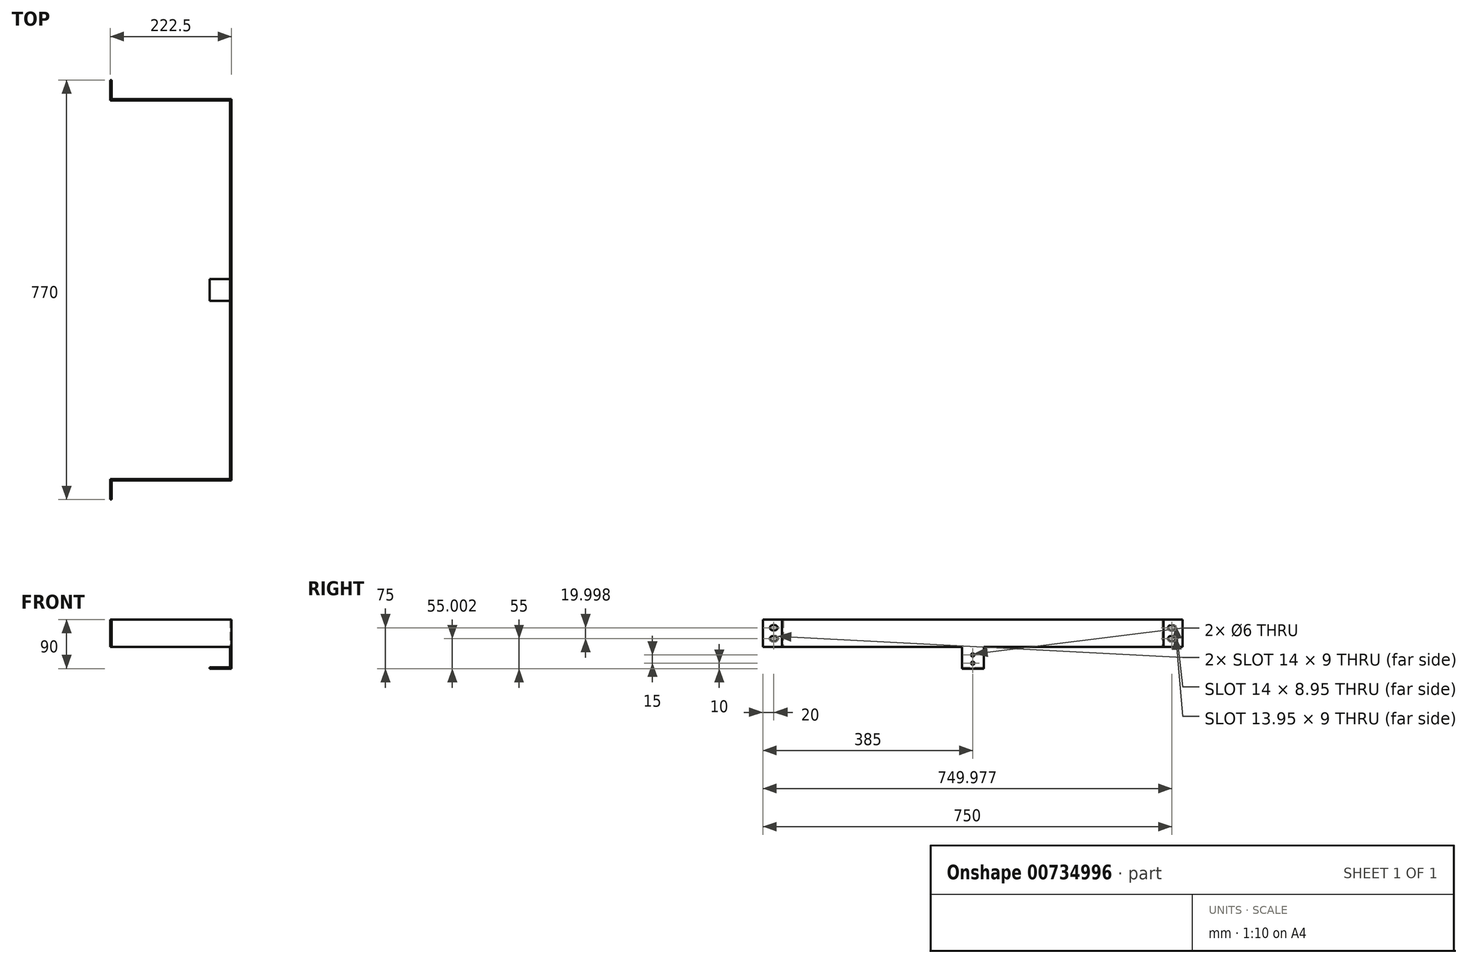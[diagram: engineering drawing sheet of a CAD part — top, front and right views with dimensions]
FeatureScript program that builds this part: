
annotation { "Feature Type Name" : "Feature", "Feature Type Description" : "" }
export const myFeature = defineFeature(function(context is Context, id is Id, definition is map)
    precondition{}
    {
        {
            var Q0;
            Q0=qCreatedBy(makeId("Top.planeOp"),FACE);
            var sketch = newSketch(context, id + "F0", { "sketchPlane" : qUnion([Q0])});
            skLineSegment(sketch, "E0", {"start": v(0, 0) * mm, "end": v(0, 350) * mm});
            skLineSegment(sketch, "E1", {"start": v(0, 350) * mm, "end": v(-220, 350) * mm});
            skLineSegment(sketch, "E2", {"start": v(-220, 350) * mm, "end": v(-220, 385) * mm});
            skLineSegment(sketch, "E3", {"start": v(-220, 385) * mm, "end": v(-222.5, 385) * mm});
            skLineSegment(sketch, "E4", {"start": v(-222.5, 385) * mm, "end": v(-222.5, 347.5) * mm});
            skLineSegment(sketch, "E5", {"start": v(-222.5, 347.5) * mm, "end": v(-2.5, 347.5) * mm});
            skLineSegment(sketch, "E6", {"start": v(-2.5, 347.5) * mm, "end": v(-2.5, 0) * mm});
            skLineSegment(sketch, "E7", {"start": v(-2.5, 0) * mm, "end": v(0, 0) * mm});
            skLineSegment(sketch, "E8.MirrorCS", {"start": v(-220, -385) * mm, "end": v(-222.5, -385) * mm});
            skLineSegment(sketch, "E9.MirrorCS", {"start": v(0, -350) * mm, "end": v(-220, -350) * mm});
            skLineSegment(sketch, "E10.MirrorCS", {"start": v(0, 0) * mm, "end": v(0, -350) * mm});
            skLineSegment(sketch, "E11.MirrorCS", {"start": v(-2.5, -347.5) * mm, "end": v(-2.5, 0) * mm});
            skLineSegment(sketch, "E12.MirrorCS", {"start": v(-220, -350) * mm, "end": v(-220, -385) * mm});
            skLineSegment(sketch, "E13.MirrorCS", {"start": v(-222.5, -347.5) * mm, "end": v(-2.5, -347.5) * mm});
            skLineSegment(sketch, "E14.MirrorCS", {"start": v(-222.5, -385) * mm, "end": v(-222.5, -347.5) * mm});
            skSolve(sketch);
        }
        {
            var Q0;
            Q0 = qSketchRegion(id + "F0", true);
            extrude(context, id + "F1", {"entities" : qUnion([Q0]), "depth" : 50 * mm, "offsetDistance" : 25 * mm});
        }
        {
            var Q0;
            Q0=qCreatedBy(makeId("Right.planeOp"),FACE);
            var sketch = newSketch(context, id + "F2", { "sketchPlane" : qUnion([Q0])});
            skLineSegment(sketch, "E15", {"start": v(0, 0) * mm, "end": v(-20, 0) * mm});
            skLineSegment(sketch, "E16", {"start": v(-20, 0) * mm, "end": v(-20, -40) * mm});
            skLineSegment(sketch, "E17", {"start": v(-20, -40) * mm, "end": v(20, -40) * mm});
            skLineSegment(sketch, "E18", {"start": v(20, -40) * mm, "end": v(20, 0) * mm});
            skLineSegment(sketch, "E19", {"start": v(20, 0) * mm, "end": v(0, 0) * mm});
            skCircle(sketch, "E20", {"center": v(0, -30) * mm, "radius": 3 * mm});
            skCircle(sketch, "E21", {"center": v(0, -15) * mm, "radius": 3 * mm});
            skSolve(sketch);
        }
        {
            var Q0;
            Q0=makeQuery(id+"F2.imprint","IMPRINT",FACE,{"disambiguationData":[TD([[makeQuery(id+"F2.imprint","IMPRINT",EDGE,{"derivedFrom":sQuery(id+"F2.wireOp",EDGE,"E15")}),1.0]])]});
            extrude(context, id + "F3", {"entities" : qUnion([Q0]), "operationType" : NewBodyOperationType.ADD, "depth" : -2.5 * mm, "offsetDistance" : 25 * mm});
        }
        {
            var Q0;
            Q0=makeQuery(id+"F1.opExtrude","SWEPT_FACE",FACE,{"disambiguationData":[OSD([sQuery(id+"F0.wireOp",EDGE,"E12.MirrorCS")])]});
            var sketch = newSketch(context, id + "F4", { "sketchPlane" : qUnion([Q0])});
            skCircle(sketch, "E22", {"center": v(-367.5, 35) * mm, "radius": 4.5 * mm});
            skCircle(sketch, "E23", {"center": v(-367.5, 15) * mm, "radius": 4.5 * mm});
            skLineSegment(sketch, "E24", {"start": v(-367.5, 35) * mm, "end": v(-362.5, 35) * mm});
            skLineSegment(sketch, "E25", {"start": v(-367.5, 15) * mm, "end": v(-362.5, 15) * mm});
            skCircle(sketch, "E26", {"center": v(-362.5, 35) * mm, "radius": 4.5 * mm});
            skCircle(sketch, "E27", {"center": v(-362.5, 15) * mm, "radius": 4.5 * mm});
            skLineSegment(sketch, "E28", {"start": v(-367.68, 39.5) * mm, "end": v(-362.5, 39.5) * mm});
            skLineSegment(sketch, "E29", {"start": v(-367.5, 30.5) * mm, "end": v(-362.5, 30.5) * mm});
            skLineSegment(sketch, "E30", {"start": v(-367.49, 19.5) * mm, "end": v(-362.5, 19.5) * mm});
            skLineSegment(sketch, "E31", {"start": v(-367.67, 10.5) * mm, "end": v(-362.33, 10.5) * mm});
            skSolve(sketch);
        }
        {
            var Q0;
            Q0 = qSketchRegion(id + "F4", true);
            var Q1;
            {var subQ0=sQuery(id+"F4.wireOp",EDGE,"E24");var subQ1=sQuery(id+"F4.wireOp",EDGE,"E22");var subQ2=makeQuery(id+"F4.imprint","INTERSECT",VERTEX,{"derivedFrom":[subQ1,subQ0]});Q1=makeQuery(id+"F4.imprint","IMPRINT",FACE,{"disambiguationData":[TD([[makeQuery(id+"F4.imprint","IMPRINT",EDGE,{"disambiguationData":[TD([[subQ2,1.0]])],"derivedFrom":subQ1}),1.0]])]});}
            var Q2;
            {var subQ0=sQuery(id+"F4.wireOp",EDGE,"E25");var subQ1=sQuery(id+"F4.wireOp",EDGE,"E23");var subQ2=makeQuery(id+"F4.imprint","INTERSECT",VERTEX,{"derivedFrom":[subQ1,subQ0]});Q2=makeQuery(id+"F4.imprint","IMPRINT",FACE,{"disambiguationData":[TD([[makeQuery(id+"F4.imprint","IMPRINT",EDGE,{"disambiguationData":[TD([[subQ2,-1.0]])],"derivedFrom":subQ1}),1.0]])]});}
            var Q3;
            {var subQ0=sQuery(id+"F4.wireOp",EDGE,"E25");var subQ1=sQuery(id+"F4.wireOp",EDGE,"E23");var subQ2=makeQuery(id+"F4.imprint","INTERSECT",VERTEX,{"derivedFrom":[subQ1,subQ0]});Q3=makeQuery(id+"F4.imprint","IMPRINT",FACE,{"disambiguationData":[TD([[makeQuery(id+"F4.imprint","IMPRINT",EDGE,{"disambiguationData":[TD([[subQ2,1.0]])],"derivedFrom":subQ1}),1.0]])]});}
            var Q4;
            {var subQ0=sQuery(id+"F4.wireOp",EDGE,"E24");var subQ1=sQuery(id+"F4.wireOp",EDGE,"E22");var subQ2=makeQuery(id+"F4.imprint","INTERSECT",VERTEX,{"derivedFrom":[subQ1,subQ0]});Q4=makeQuery(id+"F4.imprint","IMPRINT",FACE,{"disambiguationData":[TD([[makeQuery(id+"F4.imprint","IMPRINT",EDGE,{"disambiguationData":[TD([[subQ2,-1.0]])],"derivedFrom":subQ1}),1.0]])]});}
            extrude(context, id + "F5", {"entities" : qUnion([Q0, Q1, Q2, Q3, Q4]), "operationType" : NewBodyOperationType.REMOVE, "oppositeDirection" : true, "depth" : 3 * mm, "offsetDistance" : 25 * mm});
        }
        {
            var Q0;
            Q0=makeQuery(id+"F1.opExtrude","SWEPT_FACE",FACE,{"disambiguationData":[OSD([sQuery(id+"F0.wireOp",EDGE,"E2")])]});
            var sketch = newSketch(context, id + "F6", { "sketchPlane" : qUnion([Q0])});
            skPoint(sketch, "E32.endSnap0", {"position": v(367.5, 0) * mm});
            skArc(sketch, "E33", {"start": v(367.95, 30.52) * mm, "mid": v(372, 35) * mm, "end": v(367.95, 39.48) * mm});
            skArc(sketch, "E34", {"start": v(366.9, 10.54) * mm, "mid": v(371.95, 14.36) * mm, "end": v(368.18, 19.45) * mm});
            skLineSegment(sketch, "E35", {"start": v(367.5, 35) * mm, "end": v(367, 35) * mm});
            skArc(sketch, "E36", {"start": v(362.95, 39.48) * mm, "mid": v(358, 35) * mm, "end": v(362.95, 30.52) * mm});
            skArc(sketch, "E37", {"start": v(362.54, 19.5) * mm, "mid": v(358, 15) * mm, "end": v(362.54, 10.5) * mm});
            skLineSegment(sketch, "E38", {"start": v(368.18, 10.55) * mm, "end": v(362.54, 10.5) * mm});
            skLineSegment(sketch, "E39", {"start": v(362.54, 19.5) * mm, "end": v(368.18, 19.45) * mm});
            skLineSegment(sketch, "E40", {"start": v(367.95, 39.48) * mm, "end": v(362.95, 39.48) * mm});
            skLineSegment(sketch, "E41", {"start": v(362.95, 30.52) * mm, "end": v(367.95, 30.52) * mm});
            skLineSegment(sketch, "E42.trimOffspring", {"start": v(363, 35) * mm, "end": v(362.5, 35) * mm});
            skSolve(sketch);
        }
        {
            var Q0;
            Q0 = qSketchRegion(id + "F6", true);
            extrude(context, id + "F7", {"entities" : qUnion([Q0]), "operationType" : NewBodyOperationType.REMOVE, "depth" : -3 * mm, "offsetDistance" : 25 * mm});
        }
        {
            var Q0;
            Q0=makeQuery(id+"F3.boolean.opBoolean","MERGE",FACE,{"derivedFrom":[makeQuery(id+"F1.opExtrude","SWEPT_FACE",FACE,{"disambiguationData":[OSD([sQuery(id+"F0.wireOp",EDGE,"E0"),sQuery(id+"F0.wireOp",EDGE,"E10.MirrorCS")])]}),makeQuery(id+"F3.opExtrude","CAP_FACE",FACE,{"disambiguationData":[OSD([sQuery(id+"F2.wireOp",EDGE,"E15"),sQuery(id+"F2.wireOp",EDGE,"E16"),sQuery(id+"F2.wireOp",EDGE,"E17"),sQuery(id+"F2.wireOp",EDGE,"E18"),sQuery(id+"F2.wireOp",EDGE,"E19"),sQuery(id+"F2.wireOp",EDGE,"E20"),sQuery(id+"F2.wireOp",EDGE,"E21")])],"isStart":true})]});
            var sketch = newSketch(context, id + "F8", { "sketchPlane" : qUnion([Q0])});
            skLineSegment(sketch, "E43.bottom", {"start": v(-20, -40) * mm, "end": v(20, -40) * mm});
            skLineSegment(sketch, "E43.top", {"start": v(-20, -37.5) * mm, "end": v(20, -37.5) * mm});
            skLineSegment(sketch, "E43.left", {"start": v(-20, -40) * mm, "end": v(-20, -37.5) * mm});
            skLineSegment(sketch, "E43.right", {"start": v(20, -40) * mm, "end": v(20, -37.5) * mm});
            skSolve(sketch);
        }
        {
            var Q0;
            Q0 = qSketchRegion(id + "F8", true);
            extrude(context, id + "F9", {"entities" : qUnion([Q0]), "operationType" : NewBodyOperationType.ADD, "oppositeDirection" : true, "depth" : 40 * mm, "offsetDistance" : 25 * mm});
        }
        {
            var Q0;
            Q0 = qSketchRegion(id + "F6", true);
            extrude(context, id + "F10", {"entities" : qUnion([Q0]), "operationType" : NewBodyOperationType.REMOVE, "oppositeDirection" : true, "depth" : 25 * mm, "offsetDistance" : 25 * mm});
        }
    });
